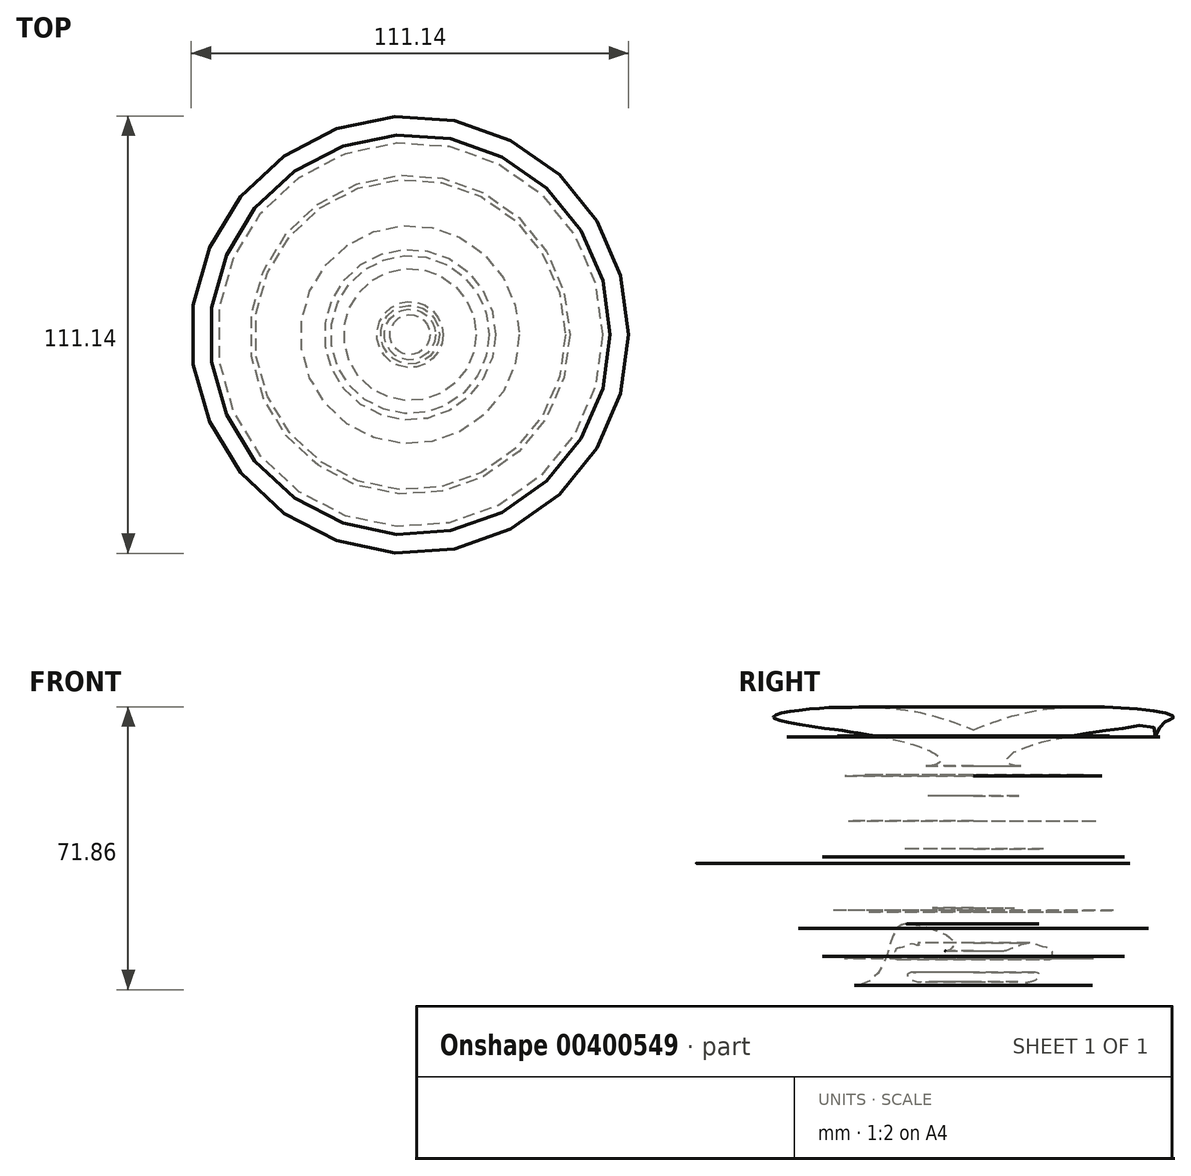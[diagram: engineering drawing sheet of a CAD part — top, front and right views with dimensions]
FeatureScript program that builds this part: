
annotation { "Feature Type Name" : "Feature", "Feature Type Description" : "" }
export const myFeature = defineFeature(function(context is Context, id is Id, definition is map)
    precondition{}
    {
        {
            var Q0;
            Q0=qCreatedBy(makeId("Front.planeOp"),FACE);
            var sketch = newSketch(context, id + "F0", { "sketchPlane" : qUnion([Q0])});
            skLineSegment(sketch, "E0", {"start": v(-57.74, 68.78) * mm, "end": v(-57.74, 2.76) * mm});
            skFitSpline(sketch, "E1", {"points": [v(-57.74, 68.78) * mm, v(-33.9, 74.5) * mm, v(-6.9, 71.93) * mm, v(-41.19, 65.43) * mm, v(-49.27, 60.7) * mm, v(-43.95, 59.71) * mm, v(-31.33, 65.43) * mm, v(-18.92, 65.62) * mm, v(-21.48, 57.74) * mm, v(-34.1, 56.76) * mm, v(-34.49, 48.87) * mm, v(-18.52, 48.48) * mm, v(-11.63, 66.6) * mm, v(-2.96, 59.71) * mm, v(-7.1, 41.78) * mm, v(-18.92, 36.46) * mm, v(-38.82, 43.36) * mm, v(-46.11, 52.03) * mm, v(-51.24, 39.8) * mm, v(-47.1, 23.65) * mm, v(-41.58, 37.84) * mm, v(-33.9, 32.71) * mm, v(-31.14, 22.47) * mm, v(-23.06, 33.1) * mm, v(-12.22, 32.71) * mm, v(-9.07, 23.25) * mm, v(-13.6, 18.33) * mm, v(-21.68, 22.86) * mm, v(-27.4, 19.12) * mm, v(-29.36, 14.39) * mm, v(-29.36, 11.04) * mm, v(-17.34, 10.84) * mm, v(-24.24, 4.53) * mm, v(-33.3, 6.7) * mm, v(-37.25, 16.36) * mm, v(-39.8, 19.31) * mm, v(-47.89, 17.93) * mm, v(-52.62, 14.78) * mm, v(-51.04, 12.61) * mm, v(-44.14, 14.58) * mm, v(-40, 13.6) * mm, v(-38.03, 13) * mm, v(-37.64, 11.43) * mm, v(-37.84, 10.64) * mm, v(-41.58, 10.64) * mm, v(-44.14, 10.64) * mm, v(-45.72, 10.64) * mm, v(-48.08, 9.85) * mm, v(-49.66, 9.07) * mm, v(-50.25, 7.88) * mm, v(-46.9, 7.3) * mm, v(-43.16, 7.1) * mm, v(-41.19, 6.9) * mm, v(-41, 6.1) * mm, v(-43.55, 4.73) * mm, v(-46.7, 4.73) * mm, v(-57.74, 2.76) * mm], "startDerivative": vector(620.98, 245.63) * mm, "endDerivative": vector(-605.49, -135.72) * mm});
            skSolve(sketch);
        }
        {
            var Q0;
            Q0=makeQuery(id+"F0.imprint","IMPRINT",FACE,{"disambiguationData":[TD([[makeQuery(id+"F0.imprint","IMPRINT",EDGE,{"derivedFrom":sQuery(id+"F0.wireOp",EDGE,"E0")}),1.0]])]});
            var Q1;
            Q1=sQuery(id+"F0.wireOp",EDGE,"E0");
            revolve(context, id + "F1", {"entities" : qUnion([Q0]), "axis" : qUnion([Q1]), "revolveType" : RevolveType.FULL});
        }
    });
